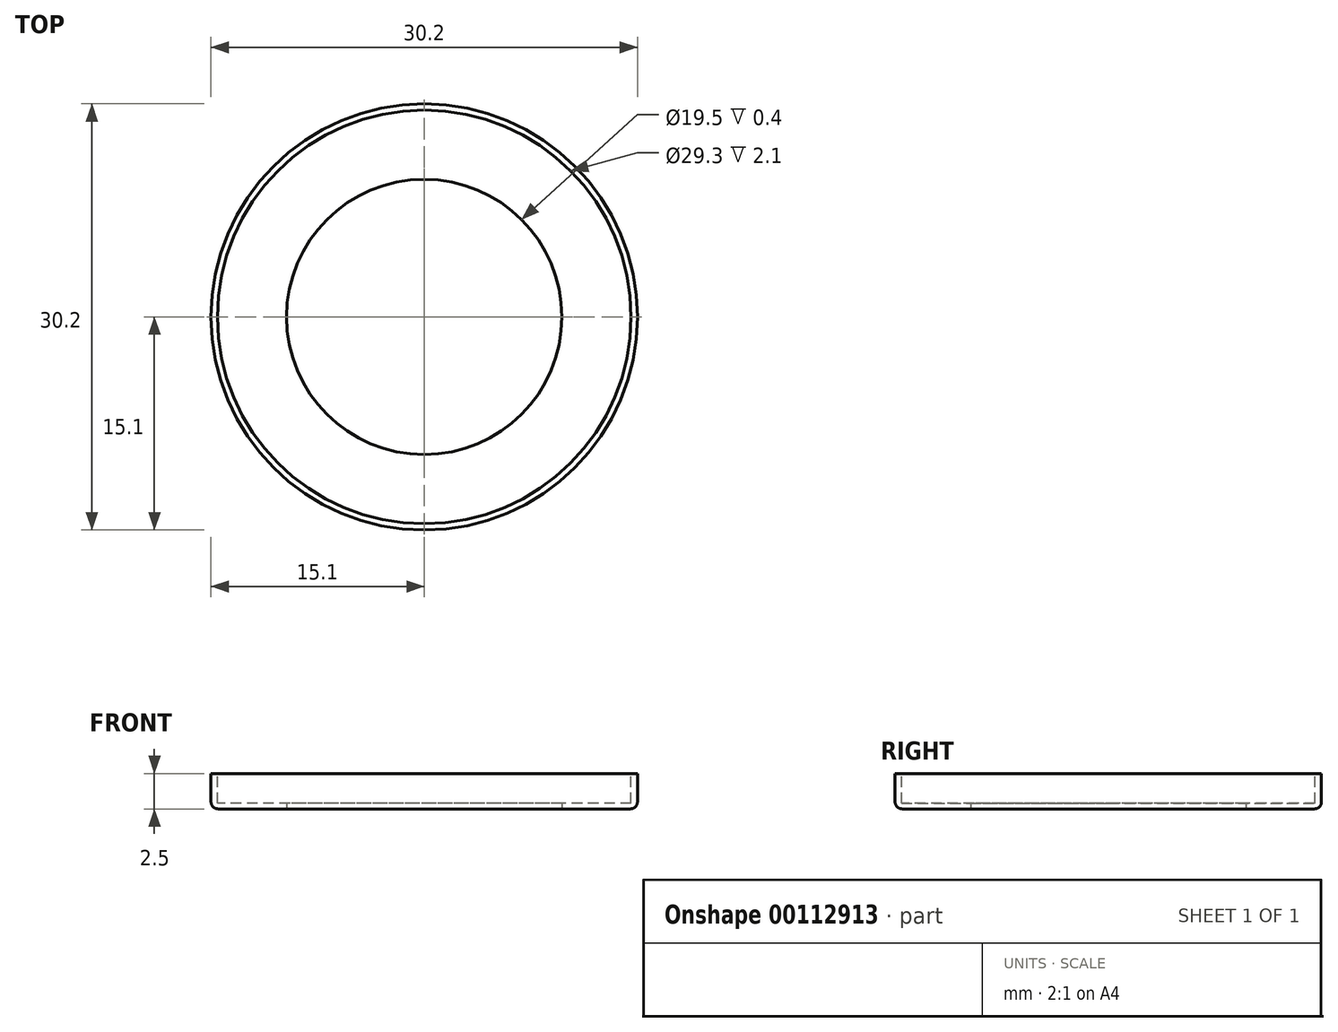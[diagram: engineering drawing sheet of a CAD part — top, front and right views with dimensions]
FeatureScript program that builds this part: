
annotation { "Feature Type Name" : "Feature", "Feature Type Description" : "" }
export const myFeature = defineFeature(function(context is Context, id is Id, definition is map)
    precondition{}
    {
        {
            var Q0;
            Q0=qCreatedBy(makeId("Top.planeOp"),FACE);
            var sketch = newSketch(context, id + "F0", { "sketchPlane" : qUnion([Q0])});
            skCircle(sketch, "E0", {"center": v(0, 0) * mm, "radius": 15.1 * mm});
            skCircle(sketch, "E1", {"center": v(0, 0) * mm, "radius": 9.75 * mm});
            skSolve(sketch);
        }
        {
            var Q0;
            Q0 = qSketchRegion(id + "F0", true);
            extrude(context, id + "F1", {"entities" : qUnion([Q0]), "depth" : 2.5 * mm});
        }
        {
            var Q0;
            Q0=makeQuery(id+"F1.opExtrude","CAP_FACE",FACE,{"disambiguationData":[OSD([sQuery(id+"F0.wireOp",EDGE,"E0"),sQuery(id+"F0.wireOp",EDGE,"E1")])],"isStart":false});
            var sketch = newSketch(context, id + "F2", { "sketchPlane" : qUnion([Q0])});
            skCircle(sketch, "E2", {"center": v(0, 0) * mm, "radius": 14.65 * mm});
            skSolve(sketch);
        }
        {
            var Q0;
            Q0 = qSketchRegion(id + "F2", true);
            extrude(context, id + "F3", {"entities" : qUnion([Q0]), "operationType" : NewBodyOperationType.REMOVE, "oppositeDirection" : true, "depth" : 2.1 * mm});
        }
        {
            var Q0;
            Q0=makeQuery(id+"F1.opExtrude","CAP_EDGE",EDGE,{"disambiguationData":[OSD([sQuery(id+"F0.wireOp",EDGE,"E0")])],"isStart":true});
            fillet(context, id + "F4", {"entities" : qUnion([Q0]), "radius" : .5 * mm, "tangentPropagation" : true, "allowEdgeOverflow" : false});
        }
    });
